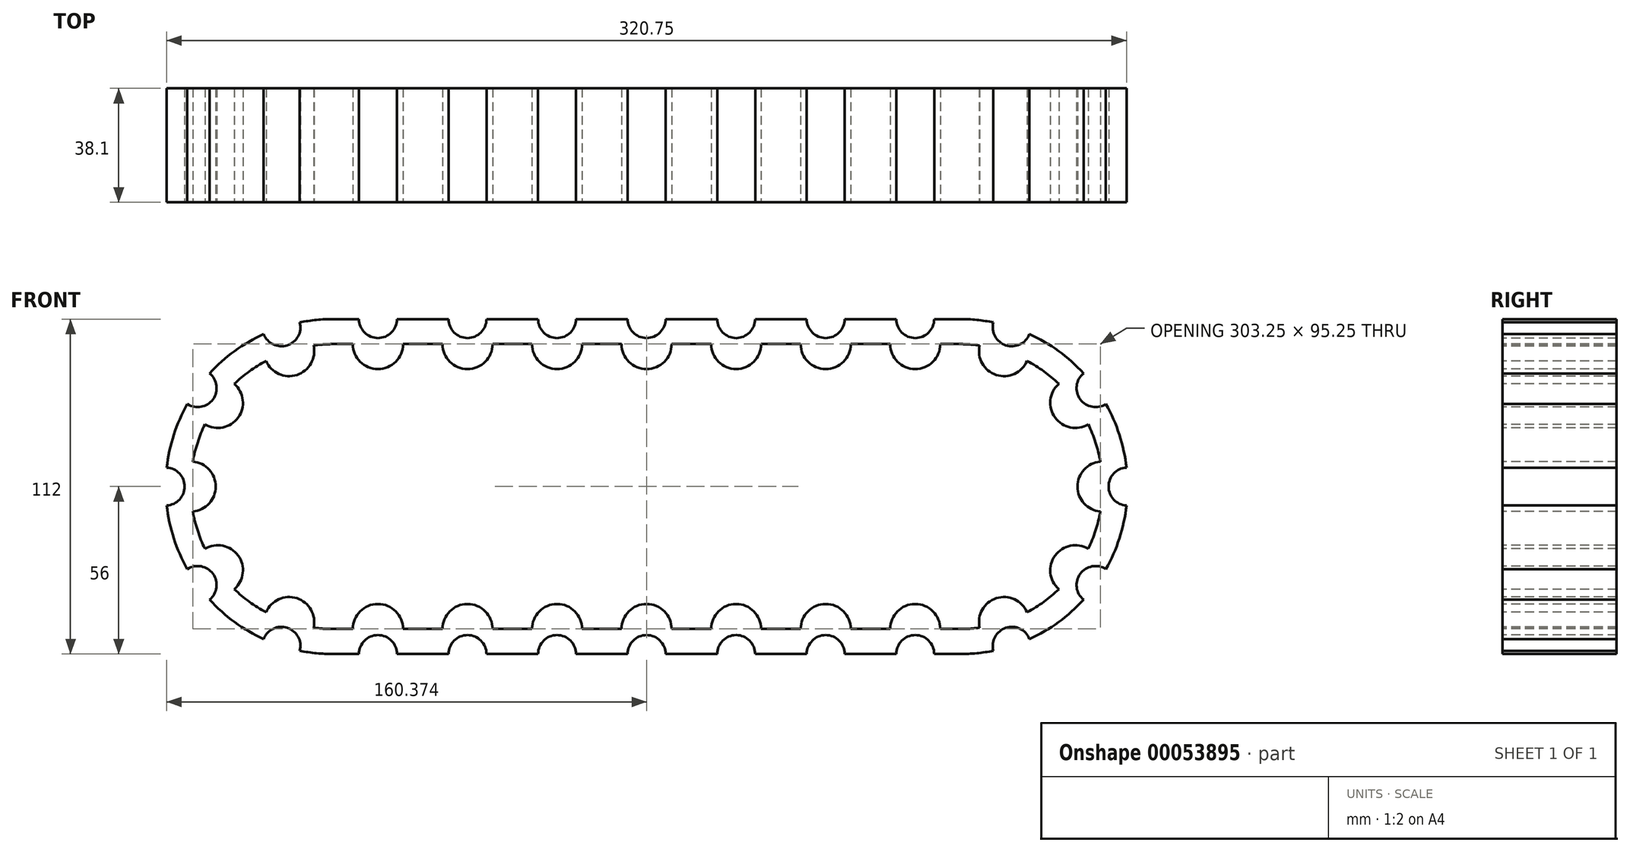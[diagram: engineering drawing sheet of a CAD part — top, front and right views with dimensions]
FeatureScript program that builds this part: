
annotation { "Feature Type Name" : "Feature", "Feature Type Description" : "" }
export const myFeature = defineFeature(function(context is Context, id is Id, definition is map)
    precondition{}
    {
        {
            var Q0;
            Q0=qCreatedBy(makeId("Front.planeOp"),FACE);
            var sketch = newSketch(context, id + "F0", { "sketchPlane" : qUnion([Q0])});
            skArc(sketch, "E0", {"start": v(-28.1, 25.72) * mm, "mid": v(-30.82, 22.4) * mm, "end": v(-33.15, 18.78) * mm});
            skCircle(sketch, "E1", {"center": v(0, 0) * mm, "radius": 9.53 * mm});
            skArc(sketch, "E2", {"start": v(5.87, 47.26) * mm, "mid": v(0, 47.63) * mm, "end": v(-5.87, 47.26) * mm});
            skLineSegment(sketch, "E3", {"start": v(-5.87, 47.26) * mm, "end": v(-7.62, 37.33) * mm});
            skLineSegment(sketch, "E4", {"start": v(5.87, 47.26) * mm, "end": v(7.62, 37.33) * mm});
            skLineSegment(sketch, "E5", {"start": v(7.62, 37.33) * mm, "end": v(-7.62, 37.33) * mm, "construction": true});
            skLineSegment(sketch, "E6", {"start": v(0, 47.63) * mm, "end": v(0, 37.33) * mm, "construction": true});
            skPoint(sketch, "E6.startSnap0", {"position": v(0, 47.63) * mm});
            skLineSegment(sketch, "E7.1.0", {"start": v(-32.53, 34.79) * mm, "end": v(-28.1, 25.72) * mm});
            skArc(sketch, "E7.1.1", {"start": v(-23.03, 41.69) * mm, "mid": v(-28, 38.53) * mm, "end": v(-32.53, 34.79) * mm});
            skLineSegment(sketch, "E7.1.2", {"start": v(-23.03, 41.69) * mm, "end": v(-15.78, 34.68) * mm});
            skLineSegment(sketch, "E7.2.0", {"start": v(-46.76, 9.02) * mm, "end": v(-37.86, 4.29) * mm});
            skArc(sketch, "E7.2.1", {"start": v(-43.14, 20.19) * mm, "mid": v(-45.3, 14.72) * mm, "end": v(-46.76, 9.02) * mm});
            skLineSegment(sketch, "E7.2.2", {"start": v(-43.14, 20.19) * mm, "end": v(-33.15, 18.78) * mm});
            skLineSegment(sketch, "E7.3.0", {"start": v(-43.14, -20.19) * mm, "end": v(-33.15, -18.78) * mm});
            skArc(sketch, "E7.3.1", {"start": v(-46.76, -9.02) * mm, "mid": v(-45.3, -14.72) * mm, "end": v(-43.14, -20.19) * mm});
            skLineSegment(sketch, "E7.3.2", {"start": v(-46.76, -9.02) * mm, "end": v(-37.86, -4.29) * mm});
            skLineSegment(sketch, "E7.4.0", {"start": v(-23.03, -41.69) * mm, "end": v(-15.78, -34.68) * mm});
            skArc(sketch, "E7.4.1", {"start": v(-32.53, -34.79) * mm, "mid": v(-28, -38.53) * mm, "end": v(-23.03, -41.69) * mm});
            skLineSegment(sketch, "E7.4.2", {"start": v(-32.53, -34.79) * mm, "end": v(-28.1, -25.72) * mm});
            skLineSegment(sketch, "E7.5.0", {"start": v(5.87, -47.26) * mm, "end": v(7.62, -37.33) * mm});
            skArc(sketch, "E7.5.1", {"start": v(-5.87, -47.26) * mm, "mid": v(0, -47.63) * mm, "end": v(5.87, -47.26) * mm});
            skLineSegment(sketch, "E7.5.2", {"start": v(-5.87, -47.26) * mm, "end": v(-7.62, -37.33) * mm});
            skLineSegment(sketch, "E7.6.0", {"start": v(32.53, -34.79) * mm, "end": v(28.1, -25.72) * mm});
            skArc(sketch, "E7.6.1", {"start": v(23.03, -41.69) * mm, "mid": v(28, -38.53) * mm, "end": v(32.53, -34.79) * mm});
            skLineSegment(sketch, "E7.6.2", {"start": v(23.03, -41.69) * mm, "end": v(15.78, -34.68) * mm});
            skLineSegment(sketch, "E7.7.0", {"start": v(46.76, -9.02) * mm, "end": v(37.86, -4.29) * mm});
            skArc(sketch, "E7.7.1", {"start": v(43.14, -20.19) * mm, "mid": v(45.3, -14.72) * mm, "end": v(46.76, -9.02) * mm});
            skLineSegment(sketch, "E7.7.2", {"start": v(43.14, -20.19) * mm, "end": v(33.15, -18.78) * mm});
            skLineSegment(sketch, "E7.8.0", {"start": v(43.14, 20.19) * mm, "end": v(33.15, 18.78) * mm});
            skArc(sketch, "E7.8.1", {"start": v(46.76, 9.02) * mm, "mid": v(45.3, 14.72) * mm, "end": v(43.14, 20.19) * mm});
            skLineSegment(sketch, "E7.8.2", {"start": v(46.76, 9.02) * mm, "end": v(37.86, 4.29) * mm});
            skLineSegment(sketch, "E7.9.0", {"start": v(23.03, 41.69) * mm, "end": v(15.78, 34.68) * mm});
            skArc(sketch, "E7.9.1", {"start": v(32.53, 34.79) * mm, "mid": v(28, 38.53) * mm, "end": v(23.03, 41.69) * mm});
            skLineSegment(sketch, "E7.9.2", {"start": v(32.53, 34.79) * mm, "end": v(28.1, 25.72) * mm});
            skArc(sketch, "E8.trimOffspring", {"start": v(-37.86, 4.29) * mm, "mid": v(-38.1, 0) * mm, "end": v(-37.86, -4.29) * mm});
            skArc(sketch, "E9.trimOffspring", {"start": v(-33.15, -18.78) * mm, "mid": v(-30.82, -22.4) * mm, "end": v(-28.1, -25.72) * mm});
            skArc(sketch, "E10.trimOffspring", {"start": v(-15.78, -34.68) * mm, "mid": v(-11.77, -36.24) * mm, "end": v(-7.62, -37.33) * mm});
            skArc(sketch, "E11.trimOffspring", {"start": v(7.62, -37.33) * mm, "mid": v(11.77, -36.24) * mm, "end": v(15.78, -34.68) * mm});
            skArc(sketch, "E12.trimOffspring", {"start": v(28.1, -25.72) * mm, "mid": v(30.82, -22.4) * mm, "end": v(33.15, -18.78) * mm});
            skArc(sketch, "E13.trimOffspring", {"start": v(37.86, -4.29) * mm, "mid": v(38.1, 0) * mm, "end": v(37.86, 4.29) * mm});
            skArc(sketch, "E14.trimOffspring", {"start": v(33.15, 18.78) * mm, "mid": v(30.82, 22.4) * mm, "end": v(28.1, 25.72) * mm});
            skArc(sketch, "E15.trimOffspring", {"start": v(15.78, 34.68) * mm, "mid": v(11.77, 36.24) * mm, "end": v(7.62, 37.33) * mm});
            skArc(sketch, "E16.trimOffspring", {"start": v(-7.62, 37.33) * mm, "mid": v(-11.77, 36.24) * mm, "end": v(-15.78, 34.68) * mm});
            skCircle(sketch, "E17", {"center": v(0, 0) * mm, "radius": 25.4 * mm, "construction": true});
            skLineSegment(sketch, "E18", {"start": v(0, 9.53) * mm, "end": v(0, 25.4) * mm, "construction": true});
            skLineSegment(sketch, "E19", {"start": v(0, 9.53) * mm, "end": v(0, 0) * mm, "construction": true});
            skCircle(sketch, "E20", {"center": v(0, 0) * mm, "radius": 15.88 * mm, "construction": true});
            skPoint(sketch, "E21", {"position": v(0, 15.88) * mm});
            skLineSegment(sketch, "E22", {"start": v(3.97, 25.09) * mm, "end": v(3.97, 8.66) * mm, "construction": true});
            skLineSegment(sketch, "E23", {"start": v(-3.97, 25.09) * mm, "end": v(-3.97, 8.66) * mm, "construction": true});
            skLineSegment(sketch, "E24", {"start": v(-3.97, 8.66) * mm, "end": v(3.97, 8.66) * mm, "construction": true});
            skLineSegment(sketch, "E25.1.0", {"start": v(-23.71, -9.1) * mm, "end": v(-9.48, -0.9) * mm, "construction": true});
            skLineSegment(sketch, "E25.1.1", {"start": v(-5.51, -7.77) * mm, "end": v(-9.48, -0.9) * mm, "construction": true});
            skLineSegment(sketch, "E25.1.2", {"start": v(-19.74, -15.98) * mm, "end": v(-5.51, -7.77) * mm, "construction": true});
            skLineSegment(sketch, "E25.1.3", {"start": v(-7.5, -4.33) * mm, "end": v(-22, -12.7) * mm, "construction": true});
            skLineSegment(sketch, "E25.2.0", {"start": v(19.74, -15.98) * mm, "end": v(5.51, -7.77) * mm, "construction": true});
            skLineSegment(sketch, "E25.2.1", {"start": v(9.48, -0.9) * mm, "end": v(5.51, -7.77) * mm, "construction": true});
            skLineSegment(sketch, "E25.2.2", {"start": v(23.71, -9.1) * mm, "end": v(9.48, -0.9) * mm, "construction": true});
            skLineSegment(sketch, "E25.2.3", {"start": v(7.5, -4.33) * mm, "end": v(22, -12.7) * mm, "construction": true});
            skPoint(sketch, "E26.orphan", {"position": v(8.25, -4.76) * mm});
            skPoint(sketch, "E27.orphan", {"position": v(-8.25, -4.76) * mm});
            skPoint(sketch, "E28.orphan", {"position": v(-3.97, 15.37) * mm});
            skPoint(sketch, "E29.orphan", {"position": v(3.97, 15.37) * mm});
            skPoint(sketch, "E30.orphan", {"position": v(15.3, -4.25) * mm});
            skPoint(sketch, "E31.orphan", {"position": v(11.33, -11.12) * mm});
            skPoint(sketch, "E32.orphan", {"position": v(-15.3, -4.25) * mm});
            skPoint(sketch, "E33.orphan", {"position": v(-11.33, -11.12) * mm});
            skSolve(sketch);
        }
        {
            var Q0;
            Q0=qCreatedBy(makeId("Front.planeOp"),FACE);
            var sketch = newSketch(context, id + "F1", { "sketchPlane" : qUnion([Q0])});
            skLineSegment(sketch, "E34", {"start": v(0, 0) * mm, "end": v(104.73, 0) * mm, "construction": true});
            skLineSegment(sketch, "E35.0", {"start": v(-23.03, 41.69) * mm, "end": v(-15.78, 34.68) * mm, "construction": true});
            skLineSegment(sketch, "E35.1", {"start": v(-5.87, 47.26) * mm, "end": v(-7.62, 37.33) * mm, "construction": true});
            skCircle(sketch, "E36", {"center": v(-14.72, 45.3) * mm, "radius": 8.37 * mm});
            skLineSegment(sketch, "E37", {"start": v(0, 0) * mm, "end": v(-14.72, 45.3) * mm, "construction": true});
            skArc(sketch, "E38.0", {"start": v(5.87, 47.26) * mm, "mid": v(0, 47.63) * mm, "end": v(-5.87, 47.26) * mm, "construction": true});
            skArc(sketch, "E39.0", {"start": v(-23.03, 41.69) * mm, "mid": v(-28, 38.53) * mm, "end": v(-32.53, 34.79) * mm, "construction": true});
            skLineSegment(sketch, "E40", {"start": v(0, 0) * mm, "end": v(-28, 38.53) * mm, "construction": true});
            skLineSegment(sketch, "E41.0", {"start": v(-32.53, 34.79) * mm, "end": v(-28.1, 25.72) * mm, "construction": true});
            skLineSegment(sketch, "E42.0", {"start": v(-43.14, 20.19) * mm, "end": v(-33.15, 18.78) * mm, "construction": true});
            skCircle(sketch, "E43", {"center": v(-38.53, 28) * mm, "radius": 8.37 * mm});
            skLineSegment(sketch, "E44", {"start": v(0, 0) * mm, "end": v(-38.53, 28) * mm, "construction": true});
            skArc(sketch, "E45", {"start": v(-14.72, 45.3) * mm, "mid": v(-28, 38.53) * mm, "end": v(-38.53, 28) * mm});
            skArc(sketch, "E46", {"start": v(-14.72, 45.3) * mm, "mid": v(-7.45, 47.04) * mm, "end": v(0, 47.63) * mm});
            skLineSegment(sketch, "E47", {"start": v(0, 47.63) * mm, "end": v(14.96, 47.63) * mm});
            skCircle(sketch, "E48", {"center": v(14.96, 47.63) * mm, "radius": 8.37 * mm});
            skLineSegment(sketch, "E49", {"start": v(0, 0) * mm, "end": v(14.96, 47.63) * mm, "construction": true});
            skLineSegment(sketch, "E50", {"start": v(104.73, 0) * mm, "end": v(104.73, -47.63) * mm, "construction": true});
            skLineSegment(sketch, "E51", {"start": v(14.96, 47.63) * mm, "end": v(44.89, 47.63) * mm});
            skCircle(sketch, "E52", {"center": v(44.89, 47.63) * mm, "radius": 8.37 * mm});
            skLineSegment(sketch, "E53.1.0.0", {"start": v(44.89, 47.63) * mm, "end": v(74.81, 47.63) * mm});
            skCircle(sketch, "E53.1.0.1", {"center": v(74.81, 47.63) * mm, "radius": 8.37 * mm});
            skLineSegment(sketch, "E53.2.0.0", {"start": v(74.81, 47.63) * mm, "end": v(104.73, 47.63) * mm});
            skCircle(sketch, "E53.2.0.1", {"center": v(104.73, 47.63) * mm, "radius": 8.37 * mm});
            skLineSegment(sketch, "E53.direction1", {"start": v(14.96, 47.63) * mm, "end": v(44.89, 47.63) * mm, "construction": true});
            skLineSegment(sketch, "E54.0", {"start": v(-46.76, -9.02) * mm, "end": v(-37.86, -4.29) * mm, "construction": true});
            skLineSegment(sketch, "E54.1", {"start": v(-46.76, 9.02) * mm, "end": v(-37.86, 4.29) * mm, "construction": true});
            skCircle(sketch, "E55", {"center": v(-47.63, 0) * mm, "radius": 8.37 * mm});
            skArc(sketch, "E56", {"start": v(-38.53, 28) * mm, "mid": v(-45.3, 14.72) * mm, "end": v(-47.63, 0) * mm});
            skCircle(sketch, "E57.MirrorC", {"center": v(14.96, -47.63) * mm, "radius": 8.37 * mm});
            skCircle(sketch, "E58.MirrorC", {"center": v(44.89, -47.63) * mm, "radius": 8.37 * mm});
            skCircle(sketch, "E59.MirrorC", {"center": v(74.81, -47.63) * mm, "radius": 8.37 * mm});
            skCircle(sketch, "E60.MirrorC", {"center": v(104.73, -47.63) * mm, "radius": 8.37 * mm});
            skCircle(sketch, "E61.MirrorC", {"center": v(-14.72, -45.3) * mm, "radius": 8.37 * mm});
            skCircle(sketch, "E62.MirrorC", {"center": v(-38.53, -28) * mm, "radius": 8.37 * mm});
            skCircle(sketch, "E63.MirrorC", {"center": v(134.66, 47.63) * mm, "radius": 8.37 * mm});
            skCircle(sketch, "E64.MirrorC", {"center": v(134.66, -47.63) * mm, "radius": 8.37 * mm});
            skCircle(sketch, "E65.MirrorC", {"center": v(164.58, 47.63) * mm, "radius": 8.37 * mm});
            skCircle(sketch, "E66.MirrorC", {"center": v(164.58, -47.62) * mm, "radius": 8.37 * mm});
            skCircle(sketch, "E67.MirrorC", {"center": v(194.5, 47.63) * mm, "radius": 8.37 * mm});
            skCircle(sketch, "E68.MirrorC", {"center": v(194.5, -47.62) * mm, "radius": 8.37 * mm});
            skCircle(sketch, "E69.MirrorC", {"center": v(224.19, 45.3) * mm, "radius": 8.37 * mm});
            skCircle(sketch, "E70.MirrorC", {"center": v(224.19, -45.3) * mm, "radius": 8.37 * mm});
            skCircle(sketch, "E71.MirrorC", {"center": v(248, 28) * mm, "radius": 8.37 * mm});
            skCircle(sketch, "E72.MirrorC", {"center": v(248, -28) * mm, "radius": 8.37 * mm});
            skCircle(sketch, "E73.MirrorC", {"center": v(257.1, 0) * mm, "radius": 8.37 * mm});
            skLineSegment(sketch, "E74", {"start": v(104.73, 47.63) * mm, "end": v(194.5, 47.63) * mm});
            skLineSegment(sketch, "E75", {"start": v(14.96, -47.63) * mm, "end": v(194.5, -47.62) * mm});
            skLineSegment(sketch, "E76", {"start": v(194.5, 47.63) * mm, "end": v(209.47, 47.63) * mm});
            skLineSegment(sketch, "E77", {"start": v(194.5, -47.62) * mm, "end": v(209.47, -47.62) * mm});
            skLineSegment(sketch, "E78", {"start": v(104.73, 0) * mm, "end": v(209.47, 0) * mm, "construction": true});
            skArc(sketch, "E79", {"start": v(-47.63, 0) * mm, "mid": v(-33.68, -33.68) * mm, "end": v(0, -47.63) * mm});
            skLineSegment(sketch, "E80", {"start": v(14.96, -47.63) * mm, "end": v(0, -47.63) * mm});
            skArc(sketch, "E81", {"start": v(209.47, 47.63) * mm, "mid": v(257.1, 0) * mm, "end": v(209.47, -47.63) * mm});
            skCircle(sketch, "E82", {"center": v(0, 0) * mm, "radius": 56 * mm});
            skCircle(sketch, "E83", {"center": v(209.47, 0) * mm, "radius": 56 * mm});
            skLineSegment(sketch, "E84", {"start": v(0, 56) * mm, "end": v(209.47, 56) * mm});
            skLineSegment(sketch, "E85", {"start": v(0, -56) * mm, "end": v(209.47, -56) * mm});
            skLineSegment(sketch, "E86", {"start": v(0, 47.63) * mm, "end": v(0, 0) * mm, "construction": true});
            skSolve(sketch);
        }
        {
            var Q0;
            Q0=qCreatedBy(makeId("Front.planeOp"),FACE);
            var sketch = newSketch(context, id + "F2", { "sketchPlane" : qUnion([Q0])});
            skLineSegment(sketch, "E87", {"start": v(0, 0) * mm, "end": v(0, 47.63) * mm, "construction": true});
            skArc(sketch, "E88", {"start": v(0, 47.63) * mm, "mid": v(-3.29, 47.51) * mm, "end": v(-6.56, 47.17) * mm});
            skArc(sketch, "E89", {"start": v(0, 56) * mm, "mid": v(-56, 0) * mm, "end": v(0, -56) * mm});
            skPoint(sketch, "E89.startSnap0", {"position": v(0, 23.81) * mm});
            skLineSegment(sketch, "E90", {"start": v(0, 47.63) * mm, "end": v(0, 56) * mm, "construction": true});
            skLineSegment(sketch, "E91", {"start": v(0, 47.63) * mm, "end": v(6.6, 47.63) * mm});
            skLineSegment(sketch, "E92.0", {"start": v(0, 0) * mm, "end": v(104.73, 0) * mm, "construction": true});
            skLineSegment(sketch, "E92.1", {"start": v(104.73, 0) * mm, "end": v(209.47, 0) * mm, "construction": true});
            skLineSegment(sketch, "E93.0", {"start": v(0, 56) * mm, "end": v(209.47, 56) * mm});
            skLineSegment(sketch, "E94.0", {"start": v(0, -56) * mm, "end": v(209.47, -56) * mm});
            skArc(sketch, "E95.MirrorCS", {"start": v(209.47, 47.63) * mm, "mid": v(212.76, 47.51) * mm, "end": v(216.03, 47.17) * mm});
            skLineSegment(sketch, "E96", {"start": v(0, -47.63) * mm, "end": v(6.6, -47.63) * mm});
            skArc(sketch, "E97.0", {"start": v(-22.42, 42.02) * mm, "mid": v(-12.13, 37.33) * mm, "end": v(-6.56, 47.17) * mm});
            skArc(sketch, "E98.0", {"start": v(6.6, 47.63) * mm, "mid": v(14.96, 39.25) * mm, "end": v(23.34, 47.63) * mm});
            skArc(sketch, "E99.0", {"start": v(36.51, 47.63) * mm, "mid": v(44.89, 39.25) * mm, "end": v(53.26, 47.63) * mm});
            skArc(sketch, "E100.0", {"start": v(66.44, 47.63) * mm, "mid": v(74.81, 39.25) * mm, "end": v(83.18, 47.63) * mm});
            skArc(sketch, "E101.0", {"start": v(96.36, 47.63) * mm, "mid": v(104.73, 39.25) * mm, "end": v(113.1, 47.63) * mm});
            skArc(sketch, "E102.0", {"start": v(143.03, 47.63) * mm, "mid": v(134.66, 39.25) * mm, "end": v(126.29, 47.63) * mm});
            skArc(sketch, "E103.0", {"start": v(172.95, 47.62) * mm, "mid": v(164.58, 39.25) * mm, "end": v(156.2, 47.63) * mm});
            skArc(sketch, "E104.0", {"start": v(202.88, 47.62) * mm, "mid": v(194.5, 39.25) * mm, "end": v(186.13, 47.63) * mm});
            skArc(sketch, "E105.0", {"start": v(231.89, 42.02) * mm, "mid": v(221.6, 37.33) * mm, "end": v(216.03, 47.17) * mm});
            skArc(sketch, "E106.0", {"start": v(252.3, 20.81) * mm, "mid": v(241.23, 23.07) * mm, "end": v(242.5, 34.3) * mm});
            skArc(sketch, "E107.0", {"start": v(256.36, -8.34) * mm, "mid": v(248.72, 0) * mm, "end": v(256.36, 8.34) * mm});
            skArc(sketch, "E108.0", {"start": v(252.3, -20.81) * mm, "mid": v(241.23, -23.07) * mm, "end": v(242.5, -34.3) * mm});
            skArc(sketch, "E109.0", {"start": v(231.89, -42.02) * mm, "mid": v(221.6, -37.33) * mm, "end": v(216.03, -47.17) * mm});
            skArc(sketch, "E110.0", {"start": v(202.88, -47.62) * mm, "mid": v(194.5, -39.25) * mm, "end": v(186.13, -47.62) * mm});
            skArc(sketch, "E111.0", {"start": v(172.95, -47.62) * mm, "mid": v(164.58, -39.25) * mm, "end": v(156.2, -47.62) * mm});
            skArc(sketch, "E112.0", {"start": v(143.03, -47.63) * mm, "mid": v(134.66, -39.25) * mm, "end": v(126.29, -47.62) * mm});
            skArc(sketch, "E113.0", {"start": v(96.36, -47.63) * mm, "mid": v(104.73, -39.25) * mm, "end": v(113.1, -47.62) * mm});
            skArc(sketch, "E114.0", {"start": v(66.44, -47.62) * mm, "mid": v(74.81, -39.25) * mm, "end": v(83.18, -47.62) * mm});
            skArc(sketch, "E115.0", {"start": v(36.51, -47.63) * mm, "mid": v(44.89, -39.25) * mm, "end": v(53.26, -47.63) * mm});
            skArc(sketch, "E116.0", {"start": v(6.6, -47.63) * mm, "mid": v(14.96, -39.25) * mm, "end": v(23.34, -47.63) * mm});
            skArc(sketch, "E117.0", {"start": v(-22.42, -42.02) * mm, "mid": v(-12.13, -37.33) * mm, "end": v(-6.56, -47.17) * mm});
            skArc(sketch, "E118.0", {"start": v(-42.84, -20.81) * mm, "mid": v(-31.76, -23.07) * mm, "end": v(-33.03, -34.3) * mm});
            skArc(sketch, "E119.0", {"start": v(-46.89, -8.34) * mm, "mid": v(-39.25, 0) * mm, "end": v(-46.89, 8.34) * mm});
            skArc(sketch, "E120.trimOffspring", {"start": v(209.47, -56) * mm, "mid": v(265.47, 0) * mm, "end": v(209.47, 56) * mm});
            skArc(sketch, "E121.0", {"start": v(-42.84, 20.81) * mm, "mid": v(-31.76, 23.07) * mm, "end": v(-33.03, 34.3) * mm});
            skLineSegment(sketch, "E122.trimOffspring", {"start": v(23.34, 47.63) * mm, "end": v(36.51, 47.63) * mm});
            skLineSegment(sketch, "E123.trimOffspring", {"start": v(53.26, 47.63) * mm, "end": v(66.44, 47.63) * mm});
            skLineSegment(sketch, "E124.trimOffspring", {"start": v(83.18, 47.63) * mm, "end": v(96.36, 47.63) * mm});
            skLineSegment(sketch, "E125.trimOffspring", {"start": v(113.1, 47.63) * mm, "end": v(126.29, 47.63) * mm});
            skLineSegment(sketch, "E126.trimOffspring", {"start": v(143.03, 47.63) * mm, "end": v(156.2, 47.63) * mm});
            skLineSegment(sketch, "E127.trimOffspring", {"start": v(172.95, 47.63) * mm, "end": v(186.13, 47.63) * mm});
            skLineSegment(sketch, "E128.trimOffspring", {"start": v(202.88, 47.63) * mm, "end": v(209.47, 47.63) * mm});
            skArc(sketch, "E129.trimOffspring", {"start": v(231.89, 42.02) * mm, "mid": v(237.46, 38.53) * mm, "end": v(242.5, 34.3) * mm});
            skArc(sketch, "E130.trimOffspring", {"start": v(252.3, 20.81) * mm, "mid": v(254.76, 14.72) * mm, "end": v(256.36, 8.34) * mm});
            skArc(sketch, "E131.trimOffspring", {"start": v(242.5, -34.3) * mm, "mid": v(237.46, -38.53) * mm, "end": v(231.89, -42.02) * mm});
            skArc(sketch, "E132.trimOffspring", {"start": v(-22.42, 42.02) * mm, "mid": v(-28, 38.53) * mm, "end": v(-33.03, 34.3) * mm});
            skArc(sketch, "E133.trimOffspring", {"start": v(-42.84, 20.81) * mm, "mid": v(-45.3, 14.72) * mm, "end": v(-46.89, 8.34) * mm});
            skArc(sketch, "E134.trimOffspring", {"start": v(-46.89, -8.34) * mm, "mid": v(-45.3, -14.72) * mm, "end": v(-42.84, -20.81) * mm});
            skArc(sketch, "E135.trimOffspring", {"start": v(-33.03, -34.3) * mm, "mid": v(-28, -38.53) * mm, "end": v(-22.42, -42.02) * mm});
            skArc(sketch, "E136.trimOffspring", {"start": v(-6.56, -47.17) * mm, "mid": v(-3.29, -47.51) * mm, "end": v(0, -47.63) * mm});
            skLineSegment(sketch, "E137.trimOffspring", {"start": v(23.34, -47.63) * mm, "end": v(36.51, -47.63) * mm});
            skLineSegment(sketch, "E138.trimOffspring", {"start": v(53.26, -47.63) * mm, "end": v(66.44, -47.63) * mm});
            skLineSegment(sketch, "E139.trimOffspring", {"start": v(83.18, -47.63) * mm, "end": v(96.36, -47.63) * mm});
            skLineSegment(sketch, "E140.trimOffspring", {"start": v(113.1, -47.63) * mm, "end": v(126.29, -47.63) * mm});
            skLineSegment(sketch, "E141.trimOffspring", {"start": v(143.03, -47.63) * mm, "end": v(156.2, -47.63) * mm});
            skLineSegment(sketch, "E142.trimOffspring", {"start": v(172.95, -47.62) * mm, "end": v(186.13, -47.62) * mm});
            skLineSegment(sketch, "E143.trimOffspring", {"start": v(202.88, -47.62) * mm, "end": v(209.47, -47.62) * mm});
            skArc(sketch, "E144.trimOffspring", {"start": v(216.03, -47.17) * mm, "mid": v(212.76, -47.51) * mm, "end": v(209.47, -47.62) * mm});
            skArc(sketch, "E145", {"start": v(252.3, -20.81) * mm, "mid": v(254.76, -14.72) * mm, "end": v(256.36, -8.34) * mm});
            skSolve(sketch);
        }
        {
            var Q0;
            Q0 = qSketchRegion(id + "F2", true);
            extrude(context, id + "F3", {"entities" : qUnion([Q0]), "oppositeDirection" : true, "depth" : 38.1 * mm});
        }
        {
            var Q0;
            Q0=makeQuery(id+"F3.opExtrude","CAP_FACE",FACE,{"disambiguationData":[OSD([sQuery(id+"F2.wireOp",EDGE,"E88"),sQuery(id+"F2.wireOp",EDGE,"E89"),sQuery(id+"F2.wireOp",EDGE,"E91"),sQuery(id+"F2.wireOp",EDGE,"E93.0"),sQuery(id+"F2.wireOp",EDGE,"E94.0"),sQuery(id+"F2.wireOp",EDGE,"E95.MirrorCS"),sQuery(id+"F2.wireOp",EDGE,"E96"),sQuery(id+"F2.wireOp",EDGE,"E97.0"),sQuery(id+"F2.wireOp",EDGE,"E98.0"),sQuery(id+"F2.wireOp",EDGE,"E99.0"),sQuery(id+"F2.wireOp",EDGE,"E100.0"),sQuery(id+"F2.wireOp",EDGE,"E101.0"),sQuery(id+"F2.wireOp",EDGE,"E102.0"),sQuery(id+"F2.wireOp",EDGE,"E103.0"),sQuery(id+"F2.wireOp",EDGE,"E104.0"),sQuery(id+"F2.wireOp",EDGE,"E105.0"),sQuery(id+"F2.wireOp",EDGE,"E106.0"),sQuery(id+"F2.wireOp",EDGE,"E107.0"),sQuery(id+"F2.wireOp",EDGE,"E108.0"),sQuery(id+"F2.wireOp",EDGE,"E109.0"),sQuery(id+"F2.wireOp",EDGE,"E110.0"),sQuery(id+"F2.wireOp",EDGE,"E111.0"),sQuery(id+"F2.wireOp",EDGE,"E112.0"),sQuery(id+"F2.wireOp",EDGE,"E113.0"),sQuery(id+"F2.wireOp",EDGE,"E114.0"),sQuery(id+"F2.wireOp",EDGE,"E115.0"),sQuery(id+"F2.wireOp",EDGE,"E116.0"),sQuery(id+"F2.wireOp",EDGE,"E117.0"),sQuery(id+"F2.wireOp",EDGE,"E118.0"),sQuery(id+"F2.wireOp",EDGE,"E119.0"),sQuery(id+"F2.wireOp",EDGE,"E120.trimOffspring"),sQuery(id+"F2.wireOp",EDGE,"E121.0"),sQuery(id+"F2.wireOp",EDGE,"E122.trimOffspring"),sQuery(id+"F2.wireOp",EDGE,"E123.trimOffspring"),sQuery(id+"F2.wireOp",EDGE,"E124.trimOffspring"),sQuery(id+"F2.wireOp",EDGE,"E125.trimOffspring"),sQuery(id+"F2.wireOp",EDGE,"E126.trimOffspring"),sQuery(id+"F2.wireOp",EDGE,"E127.trimOffspring"),sQuery(id+"F2.wireOp",EDGE,"E128.trimOffspring"),sQuery(id+"F2.wireOp",EDGE,"E129.trimOffspring"),sQuery(id+"F2.wireOp",EDGE,"E130.trimOffspring"),sQuery(id+"F2.wireOp",EDGE,"E131.trimOffspring"),sQuery(id+"F2.wireOp",EDGE,"E132.trimOffspring"),sQuery(id+"F2.wireOp",EDGE,"E133.trimOffspring"),sQuery(id+"F2.wireOp",EDGE,"E134.trimOffspring"),sQuery(id+"F2.wireOp",EDGE,"E135.trimOffspring"),sQuery(id+"F2.wireOp",EDGE,"E136.trimOffspring"),sQuery(id+"F2.wireOp",EDGE,"E137.trimOffspring"),sQuery(id+"F2.wireOp",EDGE,"E138.trimOffspring"),sQuery(id+"F2.wireOp",EDGE,"E139.trimOffspring"),sQuery(id+"F2.wireOp",EDGE,"E140.trimOffspring"),sQuery(id+"F2.wireOp",EDGE,"E141.trimOffspring"),sQuery(id+"F2.wireOp",EDGE,"E142.trimOffspring"),sQuery(id+"F2.wireOp",EDGE,"E143.trimOffspring"),sQuery(id+"F2.wireOp",EDGE,"E144.trimOffspring"),sQuery(id+"F2.wireOp",EDGE,"E145")])],"isStart":true});
            var sketch = newSketch(context, id + "F4", { "sketchPlane" : qUnion([Q0])});
            skLineSegment(sketch, "E146", {"start": v(0, 0) * mm, "end": v(-14.72, 45.3) * mm, "construction": true});
            skLineSegment(sketch, "E147", {"start": v(-14.72, 45.3) * mm, "end": v(-17.3, 53.26) * mm, "construction": true});
            skLineSegment(sketch, "E148", {"start": v(0, 0) * mm, "end": v(-38.53, 28) * mm, "construction": true});
            skLineSegment(sketch, "E149", {"start": v(-38.53, 28) * mm, "end": v(-45.3, 32.91) * mm, "construction": true});
            skLineSegment(sketch, "E150", {"start": v(0, 0) * mm, "end": v(-47.63, 0) * mm, "construction": true});
            skLineSegment(sketch, "E151", {"start": v(-47.63, 0) * mm, "end": v(-56, 0) * mm, "construction": true});
            skLineSegment(sketch, "E152.1", {"start": v(104.73, 0) * mm, "end": v(104.73, -47.63) * mm, "construction": true});
            skLineSegment(sketch, "E152.2", {"start": v(0, 0) * mm, "end": v(104.73, 0) * mm, "construction": true});
            skLineSegment(sketch, "E152.3", {"start": v(104.73, 0) * mm, "end": v(209.47, 0) * mm, "construction": true});
            skLineSegment(sketch, "E153", {"start": v(14.96, 47.63) * mm, "end": v(14.96, 56) * mm, "construction": true});
            skLineSegment(sketch, "E154", {"start": v(44.89, 47.63) * mm, "end": v(44.89, 56) * mm, "construction": true});
            skLineSegment(sketch, "E155", {"start": v(74.81, 47.63) * mm, "end": v(74.81, 56) * mm, "construction": true});
            skLineSegment(sketch, "E156", {"start": v(104.73, 47.63) * mm, "end": v(104.73, 56) * mm, "construction": true});
            skCircle(sketch, "E157", {"center": v(-17.3, 53.26) * mm, "radius": 6.35 * mm});
            skCircle(sketch, "E158", {"center": v(14.96, 56) * mm, "radius": 6.35 * mm});
            skCircle(sketch, "E159", {"center": v(44.89, 56) * mm, "radius": 6.35 * mm});
            skCircle(sketch, "E160", {"center": v(74.81, 56) * mm, "radius": 6.35 * mm});
            skCircle(sketch, "E161", {"center": v(104.73, 56) * mm, "radius": 6.35 * mm});
            skCircle(sketch, "E162", {"center": v(-45.3, 32.91) * mm, "radius": 6.35 * mm});
            skCircle(sketch, "E163", {"center": v(-56, 0) * mm, "radius": 6.35 * mm});
            skCircle(sketch, "E164.MirrorC", {"center": v(265.47, 0) * mm, "radius": 6.35 * mm});
            skCircle(sketch, "E165.MirrorC", {"center": v(254.77, 32.91) * mm, "radius": 6.35 * mm});
            skCircle(sketch, "E166.MirrorC", {"center": v(226.77, 53.26) * mm, "radius": 6.35 * mm});
            skCircle(sketch, "E167.MirrorC", {"center": v(194.5, 56) * mm, "radius": 6.35 * mm});
            skCircle(sketch, "E168.MirrorC", {"center": v(164.58, 56) * mm, "radius": 6.35 * mm});
            skCircle(sketch, "E169.MirrorC", {"center": v(134.66, 56) * mm, "radius": 6.35 * mm});
            skCircle(sketch, "E170.MirrorC", {"center": v(-45.3, -32.91) * mm, "radius": 6.35 * mm});
            skCircle(sketch, "E171.MirrorC", {"center": v(-17.3, -53.26) * mm, "radius": 6.35 * mm});
            skCircle(sketch, "E172.MirrorC", {"center": v(14.96, -56) * mm, "radius": 6.35 * mm});
            skCircle(sketch, "E173.MirrorC", {"center": v(44.89, -56) * mm, "radius": 6.35 * mm});
            skCircle(sketch, "E174.MirrorC", {"center": v(74.81, -56) * mm, "radius": 6.35 * mm});
            skCircle(sketch, "E175.MirrorC", {"center": v(104.73, -56) * mm, "radius": 6.35 * mm});
            skCircle(sketch, "E176.MirrorC", {"center": v(134.66, -56) * mm, "radius": 6.35 * mm});
            skCircle(sketch, "E177.MirrorC", {"center": v(164.58, -56) * mm, "radius": 6.35 * mm});
            skCircle(sketch, "E178.MirrorC", {"center": v(194.5, -56) * mm, "radius": 6.35 * mm});
            skCircle(sketch, "E179.MirrorC", {"center": v(226.77, -53.26) * mm, "radius": 6.35 * mm});
            skCircle(sketch, "E180.MirrorC", {"center": v(254.77, -32.91) * mm, "radius": 6.35 * mm});
            skSolve(sketch);
        }
        {
            var Q0;
            Q0 = qSketchRegion(id + "F4", true);
            extrude(context, id + "F5", {"entities" : qUnion([Q0]), "operationType" : NewBodyOperationType.REMOVE, "endBound" : BoundingType.THROUGH_ALL, "oppositeDirection" : true, "depth" : 25.4 * mm});
        }
    });
